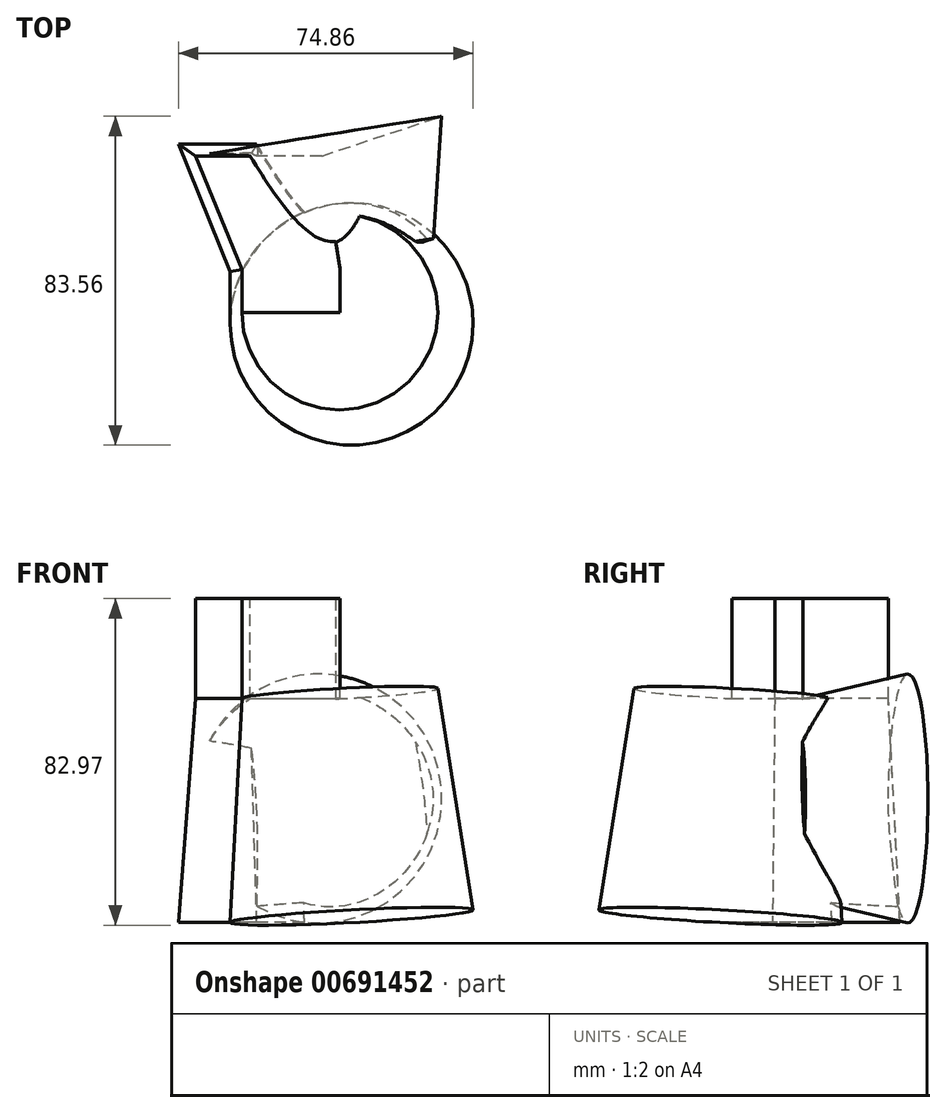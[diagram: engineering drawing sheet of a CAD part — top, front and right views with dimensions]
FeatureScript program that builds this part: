
annotation { "Feature Type Name" : "Feature", "Feature Type Description" : "" }
export const myFeature = defineFeature(function(context is Context, id is Id, definition is map)
    precondition{}
    {
        {
            var Q0;
            Q0=qCreatedBy(makeId("Top.planeOp"),FACE);
            var sketch = newSketch(context, id + "F0", { "sketchPlane" : qUnion([Q0])});
            skLineSegment(sketch, "E0", {"start": v(0, 0) * mm, "end": v(-32.05, 0) * mm});
            skLineSegment(sketch, "E1", {"start": v(-32.05, 0) * mm, "end": v(-20.33, -28.84) * mm});
            skLineSegment(sketch, "E2", {"start": v(-20.33, -28.84) * mm, "end": v(4.64, -28.84) * mm});
            skLineSegment(sketch, "E3", {"start": v(4.64, -28.84) * mm, "end": v(0, 0) * mm});
            skSolve(sketch);
        }
        {
            var Q0;
            Q0 = qSketchRegion(id + "F0", true);
            extrude(context, id + "F1", {"entities" : qUnion([Q0]), "depth" : 25.4 * mm, "offsetDistance" : 25.4 * mm});
        }
        {
            var Q0;
            Q0=makeQuery(id+"F1.opExtrude","CAP_FACE",FACE,{"disambiguationData":[OSD([sQuery(id+"F0.wireOp",EDGE,"E0"),sQuery(id+"F0.wireOp",EDGE,"E1"),sQuery(id+"F0.wireOp",EDGE,"E2"),sQuery(id+"F0.wireOp",EDGE,"E3")])],"isStart":true});
            var Q1;
            Q1=makeQuery(id+"F1.opExtrude","CAP_EDGE",EDGE,{"disambiguationData":[OSD([sQuery(id+"F0.wireOp",EDGE,"E3")])],"isStart":true});
            revolve(context, id + "F2", {"operationType" : NewBodyOperationType.ADD, "entities" : qUnion([Q0]), "axis" : qUnion([Q1]), "revolveType" : RevolveType.FULL});
        }
        {
            var Q0;
            Q0=makeQuery(id+"F1.opExtrude","SWEPT_FACE",FACE,{"disambiguationData":[OSD([sQuery(id+"F0.wireOp",EDGE,"E2")])]});
            extrude(context, id + "F3", {"entities" : qUnion([Q0]), "operationType" : NewBodyOperationType.ADD, "depth" : 10.92 * mm, "offsetDistance" : 25.4 * mm});
        }
        {
            var Q0;
            {var subQ0=sQuery(id+"F0.wireOp",EDGE,"E2");Q0=makeQuery(id+"F3.boolean.opBoolean","MERGE",FACE,{"derivedFrom":[makeQuery(id+"F1.opExtrude","CAP_FACE",FACE,{"disambiguationData":[OSD([sQuery(id+"F0.wireOp",EDGE,"E0"),sQuery(id+"F0.wireOp",EDGE,"E1"),subQ0,sQuery(id+"F0.wireOp",EDGE,"E3")])],"isStart":false}),makeQuery(id+"F3.opExtrude","SWEPT_FACE",FACE,{"disambiguationData":[OSD([subQ0]),TDD([makeQuery(id+"F1.opExtrude","CAP_EDGE",EDGE,{"disambiguationData":[OSD([subQ0])],"isStart":false})])]})]});}
            extrude(context, id + "F4", {"entities" : qUnion([Q0]), "operationType" : NewBodyOperationType.ADD, "oppositeDirection" : true, "depth" : 56.9 * mm, "offsetDistance" : 25.4 * mm, "hasDraft" : true, "draftAngle" : 3 * degree, "hasSecondDirection" : true, "secondDirectionOppositeDirection" : false, "secondDirectionDepth" : 25.4 * mm});
        }
        {
            var Q0;
            Q0=makeQuery(id+"F4.*.split.splitOp","SPLIT",FACE,{"derivedFrom":makeQuery(id+"F4.opExtrude","SWEPT_FACE",FACE,{"disambiguationData":[OSD([sQuery(id+"F0.wireOp",EDGE,"E2")])]})});
            var Q1;
            {var subQ0=sQuery(id+"F0.wireOp",EDGE,"E3");var subQ1=sQuery(id+"F0.wireOp",EDGE,"E2");Q1=makeQuery(id+"F4.*.split.splitOp","SPLIT",EDGE,{"derivedFrom":makeQuery(id+"F4.opExtrude","SWEPT_EDGE",EDGE,{"disambiguationData":[OSD([subQ1,subQ0]),TDD([makeQuery(id+"F3.opExtrude","CAP_VERTEX",VERTEX,{"disambiguationData":[OSD([subQ1,subQ0]),TDD([makeQuery(id+"F1.opExtrude","CAP_VERTEX",VERTEX,{"disambiguationData":[OSD([subQ1,subQ0])],"isStart":false})])],"isStart":false})])]})});}
            revolve(context, id + "F5", {"operationType" : NewBodyOperationType.ADD, "entities" : qUnion([Q0]), "axis" : qUnion([Q1]), "revolveType" : RevolveType.FULL});
        }
    });
